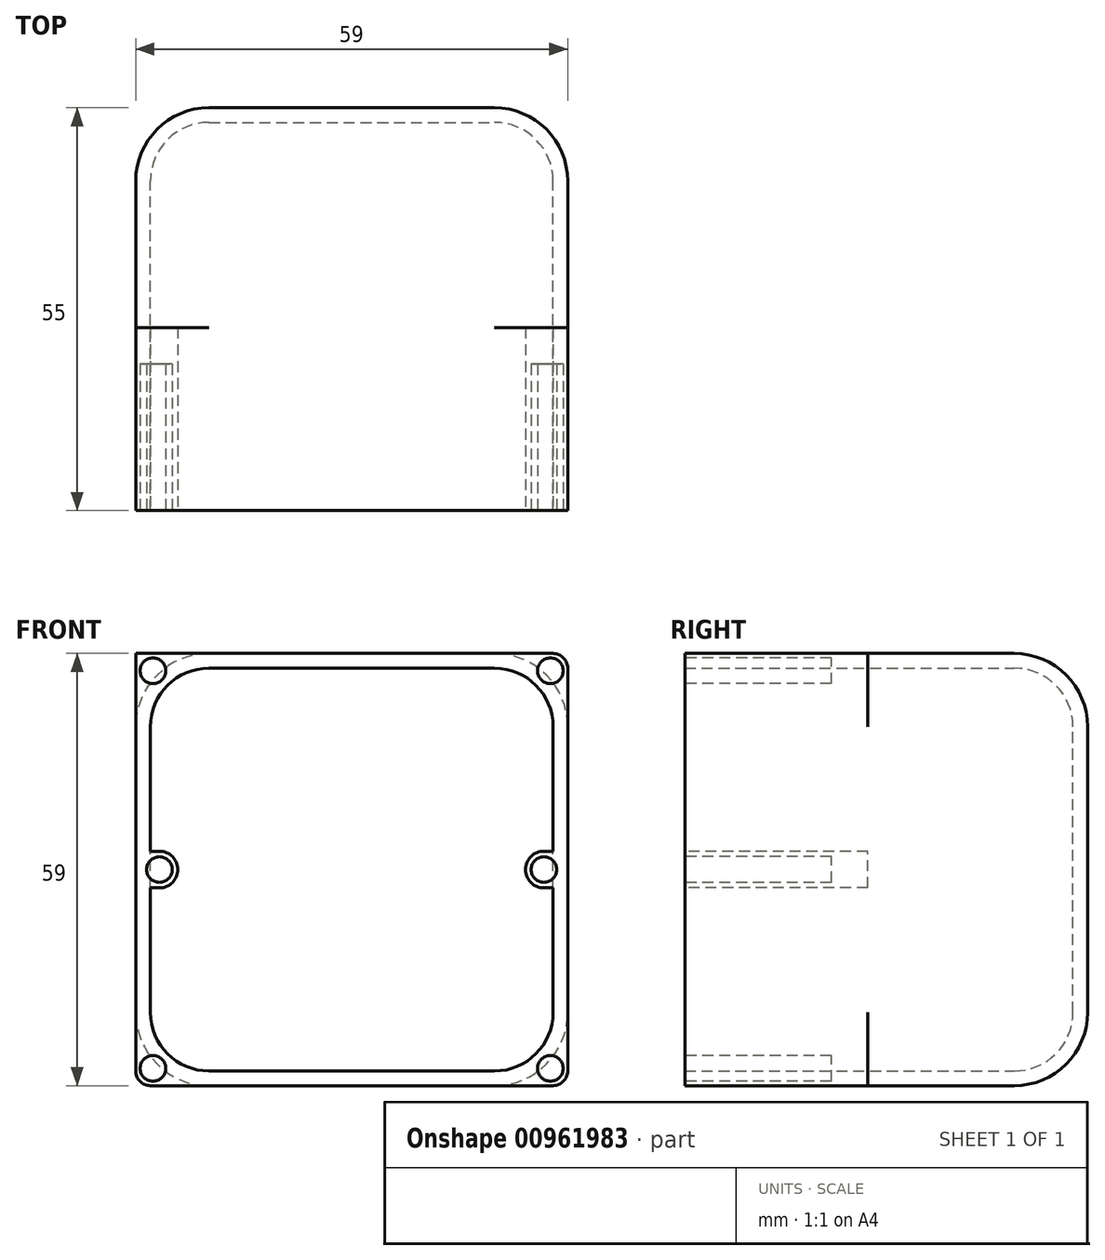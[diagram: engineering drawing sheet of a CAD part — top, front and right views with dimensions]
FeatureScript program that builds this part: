
annotation { "Feature Type Name" : "Feature", "Feature Type Description" : "" }
export const myFeature = defineFeature(function(context is Context, id is Id, definition is map)
    precondition{}
    {
        {
            var Q0;
            Q0=qCreatedBy(makeId("Front.planeOp"),FACE);
            var sketch = newSketch(context, id + "F0", { "sketchPlane" : qUnion([Q0])});
            skLineSegment(sketch, "E0.bottom", {"start": v(29.5, -29.5) * mm, "end": v(-29.5, -29.5) * mm});
            skLineSegment(sketch, "E0.top", {"start": v(29.5, 29.5) * mm, "end": v(-29.5, 29.5) * mm});
            skLineSegment(sketch, "E0.left", {"start": v(29.5, -29.5) * mm, "end": v(29.5, 29.5) * mm});
            skLineSegment(sketch, "E0.right", {"start": v(-29.5, -29.5) * mm, "end": v(-29.5, 29.5) * mm});
            skPoint(sketch, "E0.middle", {"position": v(0, 0) * mm});
            skSolve(sketch);
        }
        {
            var Q0;
            Q0=makeQuery(id+"F0.imprint","IMPRINT",FACE,{"disambiguationData":[TD([[makeQuery(id+"F0.imprint","IMPRINT",EDGE,{"derivedFrom":sQuery(id+"F0.wireOp",EDGE,"E0.bottom")}),-1.0]])]});
            extrude(context, id + "F1", {"entities" : qUnion([Q0]), "depth" : 55 * mm, "offsetDistance" : 25 * mm});
        }
        {
            var Q0;
            Q0=makeQuery(id+"F1.opExtrude","SWEPT_EDGE",EDGE,{"disambiguationData":[OSD([sQuery(id+"F0.wireOp",EDGE,"E0.top"),sQuery(id+"F0.wireOp",EDGE,"E0.right")])]});
            var Q1;
            Q1=makeQuery(id+"F1.opExtrude","SWEPT_EDGE",EDGE,{"disambiguationData":[OSD([sQuery(id+"F0.wireOp",EDGE,"E0.top"),sQuery(id+"F0.wireOp",EDGE,"E0.left")])]});
            var Q2;
            Q2=makeQuery(id+"F1.opExtrude","SWEPT_EDGE",EDGE,{"disambiguationData":[OSD([sQuery(id+"F0.wireOp",EDGE,"E0.bottom"),sQuery(id+"F0.wireOp",EDGE,"E0.left")])]});
            var Q3;
            Q3=makeQuery(id+"F1.opExtrude","SWEPT_EDGE",EDGE,{"disambiguationData":[OSD([sQuery(id+"F0.wireOp",EDGE,"E0.bottom"),sQuery(id+"F0.wireOp",EDGE,"E0.right")])]});
            var Q4;
            Q4=makeQuery(id+"F1.opExtrude","CAP_EDGE",EDGE,{"disambiguationData":[OSD([sQuery(id+"F0.wireOp",EDGE,"E0.left")])],"isStart":true});
            var Q5;
            Q5=makeQuery(id+"F1.opExtrude","CAP_EDGE",EDGE,{"disambiguationData":[OSD([sQuery(id+"F0.wireOp",EDGE,"E0.top")])],"isStart":true});
            var Q6;
            Q6=makeQuery(id+"F1.opExtrude","CAP_EDGE",EDGE,{"disambiguationData":[OSD([sQuery(id+"F0.wireOp",EDGE,"E0.bottom")])],"isStart":true});
            var Q7;
            Q7=makeQuery(id+"F1.opExtrude","CAP_FACE",FACE,{"disambiguationData":[OSD([sQuery(id+"F0.wireOp",EDGE,"E0.bottom"),sQuery(id+"F0.wireOp",EDGE,"E0.top"),sQuery(id+"F0.wireOp",EDGE,"E0.left"),sQuery(id+"F0.wireOp",EDGE,"E0.right")])],"isStart":true});
            fillet(context, id + "F2", {"entities" : qUnion([Q0, Q1, Q2, Q3, Q4, Q5, Q6, Q7]), "radius" : 10 * mm, "tangentPropagation" : true, "allowEdgeOverflow" : false});
        }
        {
            var Q0;
            Q0=makeQuery(id+"F1.opExtrude","CAP_FACE",FACE,{"disambiguationData":[OSD([sQuery(id+"F0.wireOp",EDGE,"E0.bottom"),sQuery(id+"F0.wireOp",EDGE,"E0.top"),sQuery(id+"F0.wireOp",EDGE,"E0.left"),sQuery(id+"F0.wireOp",EDGE,"E0.right")])],"isStart":false});
            shell(context, id + "F3", {"entities" : qUnion([Q0]), "thickness" : 2 * mm});
        }
        {
            var Q0;
            Q0=makeQuery(id+"F1.opExtrude","CAP_FACE",FACE,{"disambiguationData":[OSD([sQuery(id+"F0.wireOp",EDGE,"E0.bottom"),sQuery(id+"F0.wireOp",EDGE,"E0.top"),sQuery(id+"F0.wireOp",EDGE,"E0.left"),sQuery(id+"F0.wireOp",EDGE,"E0.right")])],"isStart":false});
            var sketch = newSketch(context, id + "F4", { "sketchPlane" : qUnion([Q0])});
            skLineSegment(sketch, "E1", {"start": v(29.5, 0) * mm, "end": v(-29.5, 0) * mm, "construction": true});
            skLineSegment(sketch, "E2", {"start": v(0, 29.5) * mm, "end": v(0, -29.5) * mm, "construction": true});
            skLineSegment(sketch, "E3", {"start": v(0, 0) * mm, "end": v(-26.57, 26.57) * mm, "construction": true});
            skLineSegment(sketch, "E4", {"start": v(-26.57, 26.57) * mm, "end": v(-42.28, 42.28) * mm, "construction": true});
            skArc(sketch, "E5.0", {"start": v(-19.5, 29.5) * mm, "mid": v(-26.57, 26.57) * mm, "end": v(-29.5, 19.5) * mm});
            skLineSegment(sketch, "E6", {"start": v(-19.5, 29.5) * mm, "end": v(-29.5, 29.5) * mm});
            skLineSegment(sketch, "E7", {"start": v(-29.5, 29.5) * mm, "end": v(-29.5, 19.5) * mm});
            skArc(sketch, "E8.MirrorCS", {"start": v(19.5, 29.5) * mm, "mid": v(26.57, 26.57) * mm, "end": v(29.5, 19.5) * mm});
            skLineSegment(sketch, "E9.MirrorCS", {"start": v(19.5, 29.5) * mm, "end": v(29.5, 29.5) * mm});
            skLineSegment(sketch, "E10.MirrorCS", {"start": v(29.5, 29.5) * mm, "end": v(29.5, 19.5) * mm});
            skLineSegment(sketch, "E11.MirrorCS", {"start": v(-29.5, 29.5) * mm, "end": v(-19.5, 29.5) * mm});
            skArc(sketch, "E12.MirrorCS", {"start": v(-29.5, 19.5) * mm, "mid": v(-26.57, 26.57) * mm, "end": v(-19.5, 29.5) * mm});
            skLineSegment(sketch, "E13.MirrorCS", {"start": v(-29.5, -29.5) * mm, "end": v(-19.5, -29.5) * mm});
            skLineSegment(sketch, "E14.MirrorCS", {"start": v(-29.5, -19.5) * mm, "end": v(-29.5, -29.5) * mm});
            skArc(sketch, "E15.MirrorCS", {"start": v(-29.5, -19.5) * mm, "mid": v(-26.57, -26.57) * mm, "end": v(-19.5, -29.5) * mm});
            skLineSegment(sketch, "E16.MirrorCS", {"start": v(-29.5, 19.5) * mm, "end": v(-29.5, 29.5) * mm});
            skLineSegment(sketch, "E17.MirrorCS", {"start": v(0, -29.5) * mm, "end": v(0, 29.5) * mm, "construction": true});
            skArc(sketch, "E18.MirrorCS", {"start": v(19.5, -29.5) * mm, "mid": v(26.57, -26.57) * mm, "end": v(29.5, -19.5) * mm});
            skLineSegment(sketch, "E19.MirrorCS", {"start": v(19.5, -29.5) * mm, "end": v(29.5, -29.5) * mm});
            skLineSegment(sketch, "E20.MirrorCS", {"start": v(29.5, -29.5) * mm, "end": v(29.5, -19.5) * mm});
            skArc(sketch, "E21", {"start": v(-26.25, -2.5) * mm, "mid": v(-23.75, 0) * mm, "end": v(-26.25, 2.5) * mm});
            skLineSegment(sketch, "E22", {"start": v(-26.25, -2.5) * mm, "end": v(-27.5, -2.5) * mm});
            skLineSegment(sketch, "E23", {"start": v(-26.25, 2.5) * mm, "end": v(-27.5, 2.5) * mm});
            skLineSegment(sketch, "E24", {"start": v(-27.5, 2.5) * mm, "end": v(-27.5, -2.5) * mm});
            skLineSegment(sketch, "E25.MirrorCS", {"start": v(26.25, -2.5) * mm, "end": v(27.5, -2.5) * mm});
            skLineSegment(sketch, "E26.MirrorCS", {"start": v(27.5, 2.5) * mm, "end": v(27.5, -2.5) * mm});
            skArc(sketch, "E27.MirrorCS", {"start": v(26.25, -2.5) * mm, "mid": v(23.75, 0) * mm, "end": v(26.25, 2.5) * mm});
            skLineSegment(sketch, "E28.MirrorCS", {"start": v(26.25, 2.5) * mm, "end": v(27.5, 2.5) * mm});
            skSolve(sketch);
        }
        {
            var Q0;
            Q0 = qSketchRegion(id + "F4", true);
            extrude(context, id + "F5", {"entities" : qUnion([Q0]), "operationType" : NewBodyOperationType.ADD, "oppositeDirection" : true, "depth" : 25 * mm, "offsetDistance" : 25 * mm});
        }
        {
            var Q0;
            Q0=makeQuery(id+"F5.boolean.opBoolean","MERGE",FACE,{"derivedFrom":[makeQuery(id+"F1.opExtrude","CAP_FACE",FACE,{"disambiguationData":[OSD([sQuery(id+"F0.wireOp",EDGE,"E0.bottom"),sQuery(id+"F0.wireOp",EDGE,"E0.top"),sQuery(id+"F0.wireOp",EDGE,"E0.left"),sQuery(id+"F0.wireOp",EDGE,"E0.right")])],"isStart":false}),makeQuery(id+"F5.opExtrude","CAP_FACE",FACE,{"disambiguationData":[OSD([sQuery(id+"F4.wireOp",EDGE,"E8.MirrorCS"),sQuery(id+"F4.wireOp",EDGE,"E9.MirrorCS"),sQuery(id+"F4.wireOp",EDGE,"E10.MirrorCS")])],"isStart":true}),makeQuery(id+"F5.opExtrude","CAP_FACE",FACE,{"disambiguationData":[OSD([sQuery(id+"F4.wireOp",EDGE,"E11.MirrorCS"),sQuery(id+"F4.wireOp",EDGE,"E12.MirrorCS"),sQuery(id+"F4.wireOp",EDGE,"E16.MirrorCS")])],"isStart":true}),makeQuery(id+"F5.opExtrude","CAP_FACE",FACE,{"disambiguationData":[OSD([sQuery(id+"F4.wireOp",EDGE,"E13.MirrorCS"),sQuery(id+"F4.wireOp",EDGE,"E14.MirrorCS"),sQuery(id+"F4.wireOp",EDGE,"E15.MirrorCS")])],"isStart":true}),makeQuery(id+"F5.opExtrude","CAP_FACE",FACE,{"disambiguationData":[OSD([sQuery(id+"F4.wireOp",EDGE,"E18.MirrorCS"),sQuery(id+"F4.wireOp",EDGE,"E19.MirrorCS"),sQuery(id+"F4.wireOp",EDGE,"E20.MirrorCS")])],"isStart":true})]});
            var sketch = newSketch(context, id + "F6", { "sketchPlane" : qUnion([Q0])});
            skLineSegment(sketch, "E29", {"start": v(25.16, 25.16) * mm, "end": v(29.5, 29.5) * mm, "construction": true});
            skCircle(sketch, "E30", {"center": v(27.14, 27.14) * mm, "radius": 1.75 * mm});
            skLineSegment(sketch, "E31", {"start": v(27.5, -11) * mm, "end": v(-27.5, -11) * mm, "construction": true});
            skLineSegment(sketch, "E32", {"start": v(0, 27.5) * mm, "end": v(0, -27.5) * mm, "construction": true});
            skCircle(sketch, "E33.MirrorC", {"center": v(27.14, -27.14) * mm, "radius": 1.75 * mm});
            skCircle(sketch, "E34.MirrorC", {"center": v(-27.14, -27.14) * mm, "radius": 1.75 * mm});
            skCircle(sketch, "E35.MirrorC", {"center": v(-27.14, 27.14) * mm, "radius": 1.75 * mm});
            skCircle(sketch, "E36", {"center": v(-26.25, 0) * mm, "radius": 1.75 * mm});
            skCircle(sketch, "E37", {"center": v(26.25, 0) * mm, "radius": 1.75 * mm});
            skSolve(sketch);
        }
        {
            var Q0;
            Q0 = qSketchRegion(id + "F6", true);
            extrude(context, id + "F7", {"entities" : qUnion([Q0]), "operationType" : NewBodyOperationType.REMOVE, "oppositeDirection" : true, "depth" : 20 * mm, "offsetDistance" : 25 * mm});
        }
        {
            var Q0;
            Q0=makeQuery(id+"F5.opExtrude","SWEPT_EDGE",EDGE,{"disambiguationData":[OSD([sQuery(id+"F4.wireOp",EDGE,"E9.MirrorCS"),sQuery(id+"F4.wireOp",EDGE,"E10.MirrorCS")])]});
            var Q1;
            Q1=makeQuery(id+"F5.opExtrude","SWEPT_EDGE",EDGE,{"disambiguationData":[OSD([sQuery(id+"F4.wireOp",EDGE,"E19.MirrorCS"),sQuery(id+"F4.wireOp",EDGE,"E20.MirrorCS")])]});
            var Q2;
            Q2=makeQuery(id+"F5.opExtrude","SWEPT_EDGE",EDGE,{"disambiguationData":[OSD([sQuery(id+"F4.wireOp",EDGE,"E11.MirrorCS"),sQuery(id+"F4.wireOp",EDGE,"E16.MirrorCS")])]});
            var Q3;
            Q3=makeQuery(id+"F5.opExtrude","SWEPT_EDGE",EDGE,{"disambiguationData":[OSD([sQuery(id+"F4.wireOp",EDGE,"E13.MirrorCS"),sQuery(id+"F4.wireOp",EDGE,"E14.MirrorCS")])]});
            fillet(context, id + "F8", {"entities" : qUnion([Q0, Q1, Q2, Q3]), "radius" : 2 * mm, "tangentPropagation" : true, "allowEdgeOverflow" : false});
        }
    });
